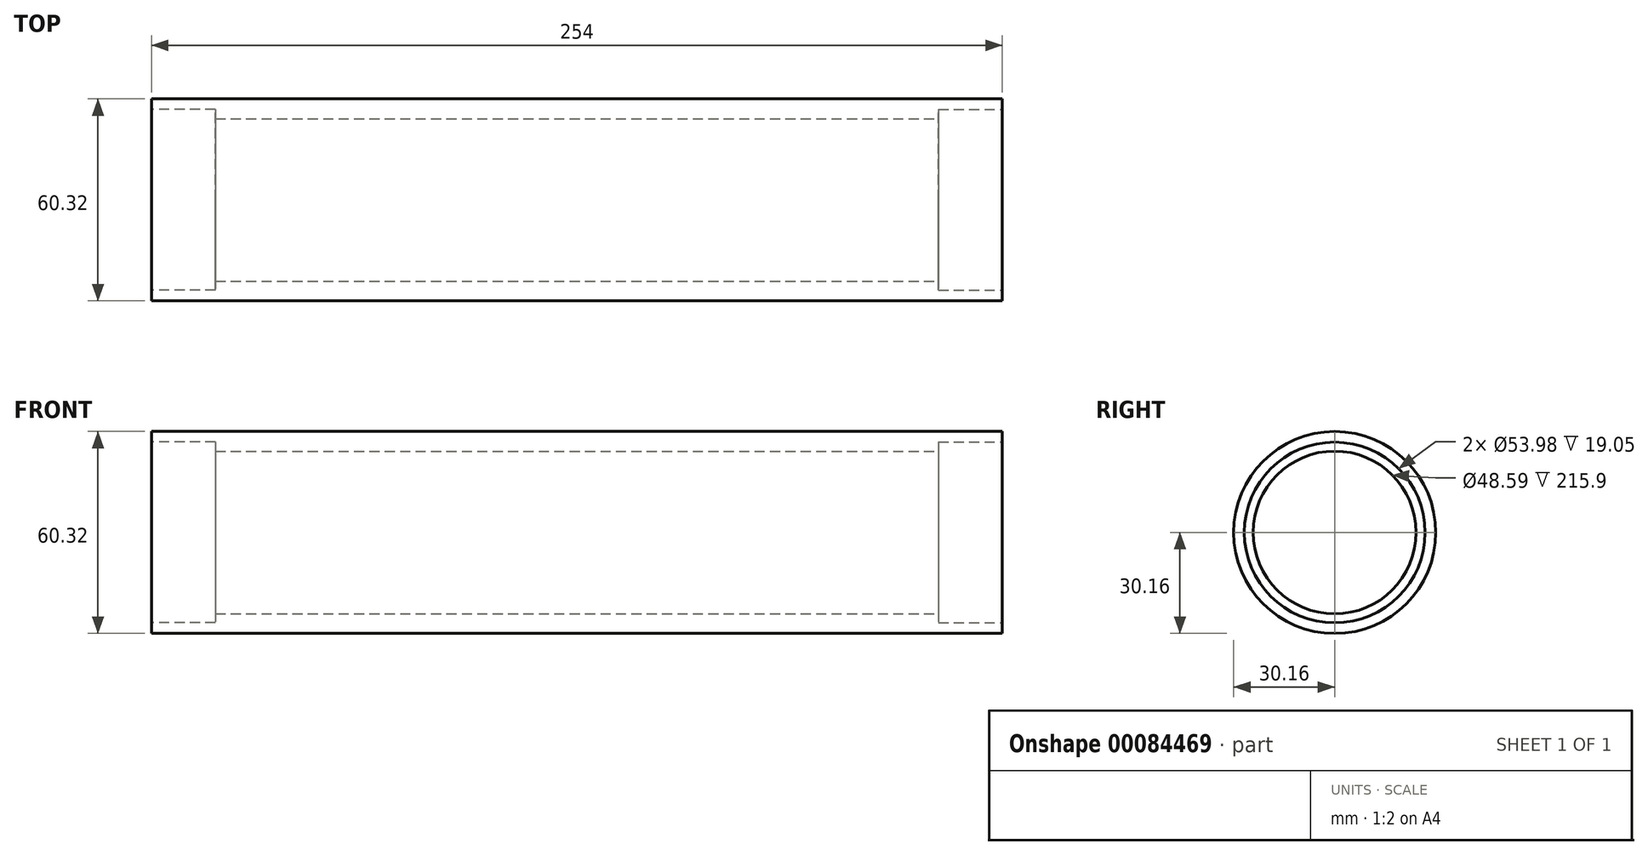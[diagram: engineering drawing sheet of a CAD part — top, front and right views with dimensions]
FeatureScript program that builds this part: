
annotation { "Feature Type Name" : "Feature", "Feature Type Description" : "" }
export const myFeature = defineFeature(function(context is Context, id is Id, definition is map)
    precondition{}
    {
        {
            var Q0;
            Q0=qCreatedBy(makeId("Front.planeOp"),FACE);
            var sketch = newSketch(context, id + "F0", { "sketchPlane" : qUnion([Q0])});
            skLineSegment(sketch, "E0", {"start": v(0, 0) * mm, "end": v(-127, 0) * mm, "construction": true});
            skLineSegment(sketch, "E1", {"start": v(0, 24.3) * mm, "end": v(-127, 24.3) * mm});
            skLineSegment(sketch, "E2", {"start": v(-127, 24.3) * mm, "end": v(-127, 30.16) * mm});
            skLineSegment(sketch, "E3", {"start": v(-127, 30.16) * mm, "end": v(0, 30.16) * mm});
            skLineSegment(sketch, "E4", {"start": v(0, 24.3) * mm, "end": v(0, 30.16) * mm});
            skSolve(sketch);
        }
        {
            var Q0;
            Q0 = qSketchRegion(id + "F0", true);
            var Q1;
            Q1=sQuery(id+"F0.wireOp",EDGE,"E0");
            revolve(context, id + "F1", {"entities" : qUnion([Q0]), "axis" : qUnion([Q1]), "revolveType" : RevolveType.FULL});
        }
        {
            var Q0;
            Q0=makeQuery(id+"F1.opRevolve","SWEPT_FACE",FACE,{"disambiguationData":[OSD([sQuery(id+"F0.wireOp",EDGE,"E2")])]});
            var sketch = newSketch(context, id + "F2", { "sketchPlane" : qUnion([Q0])});
            skCircle(sketch, "E5", {"center": v(0, 0) * mm, "radius": 26.99 * mm});
            skSolve(sketch);
        }
        {
            var Q0;
            Q0 = qSketchRegion(id + "F2", true);
            extrude(context, id + "F3", {"entities" : qUnion([Q0]), "operationType" : NewBodyOperationType.REMOVE, "oppositeDirection" : true, "depth" : 19.05 * mm});
        }
        {
            var Q0;
            Q0=makeQuery(id+"F1.opRevolve","SWEPT_BODY",BODY,{"disambiguationData":[OSD([sQuery(id+"F0.wireOp",EDGE,"E1"),sQuery(id+"F0.wireOp",EDGE,"E2"),sQuery(id+"F0.wireOp",EDGE,"E3"),sQuery(id+"F0.wireOp",EDGE,"aZSX35s8-WoIg-F6zi-F4Z4-igY9V5fxDP6z")])]});
            var Q1;
            Q1=qCreatedBy(makeId("Right.planeOp"),FACE);
            mirror(context, id + "F4", {"operationType" : NewBodyOperationType.ADD, "entities" : qUnion([Q0]), "mirrorPlane" : qUnion([Q1])});
        }
    });
